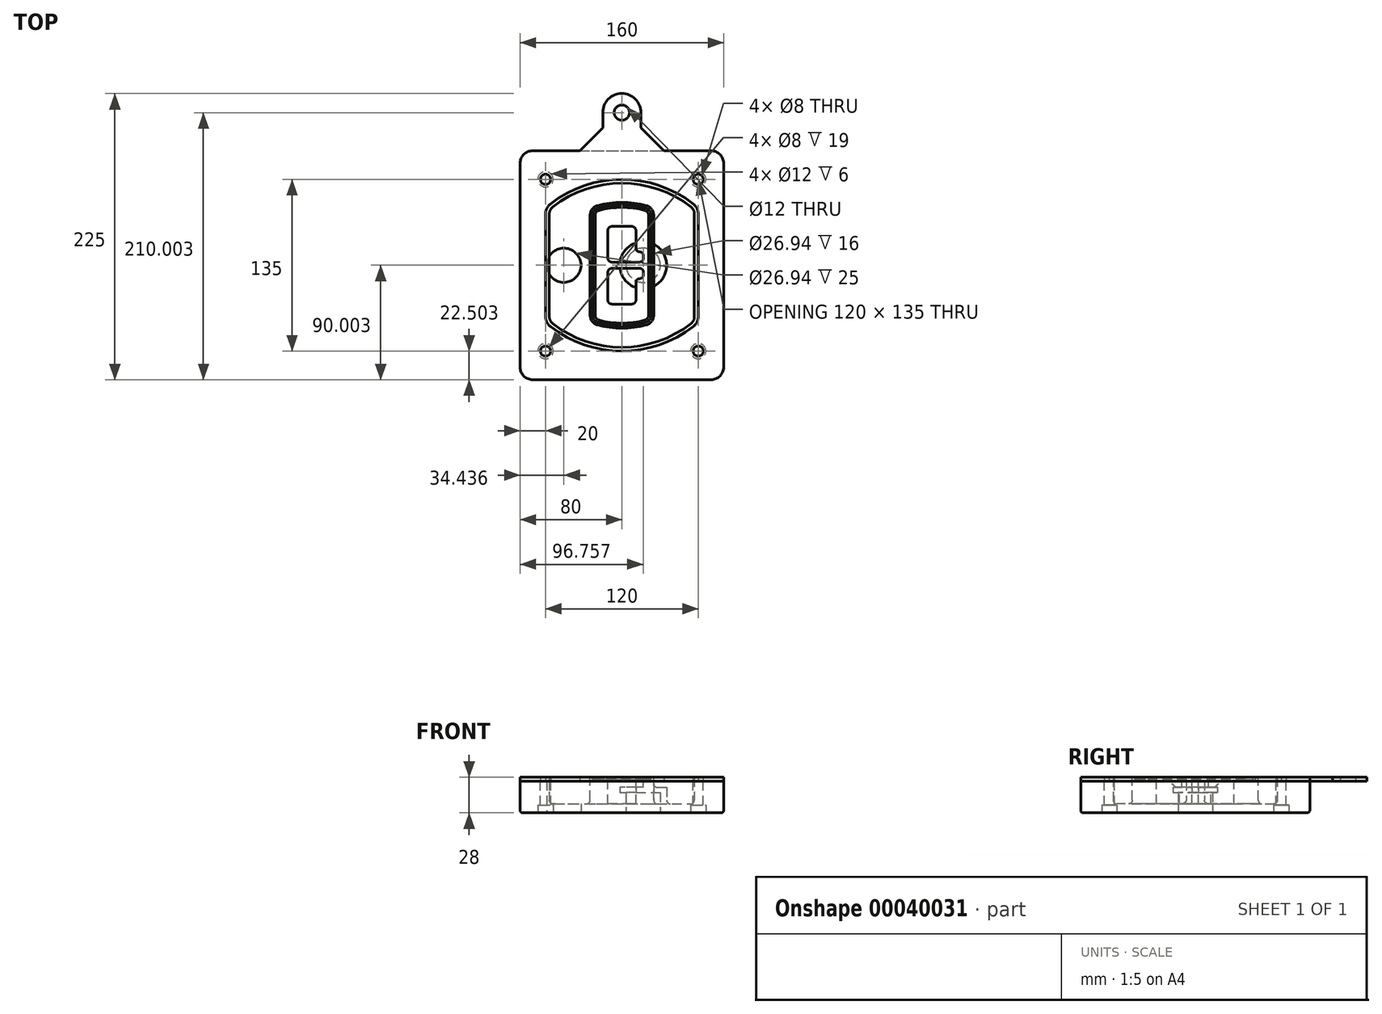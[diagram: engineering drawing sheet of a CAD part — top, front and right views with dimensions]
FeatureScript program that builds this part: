
annotation { "Feature Type Name" : "Feature", "Feature Type Description" : "" }
export const myFeature = defineFeature(function(context is Context, id is Id, definition is map)
    precondition{}
    {
        {
            var Q0;
            Q0=qCreatedBy(makeId("Top.planeOp"),FACE);
            var sketch = newSketch(context, id + "F0", { "sketchPlane" : qUnion([Q0])});
            skPoint(sketch, "E0.rect.middle", {"position": v(0, 0) * mm});
            skLineSegment(sketch, "E1.bottom", {"start": v(24.05, 28.38) * mm, "end": v(164.05, 28.38) * mm});
            skLineSegment(sketch, "E1.top", {"start": v(24.05, 208.38) * mm, "end": v(164.05, 208.38) * mm});
            skLineSegment(sketch, "E1.left", {"start": v(14.05, 38.38) * mm, "end": v(14.05, 198.38) * mm});
            skLineSegment(sketch, "E1.right", {"start": v(174.05, 38.38) * mm, "end": v(174.05, 198.38) * mm});
            skLineSegment(sketch, "E2", {"start": v(14.05, 208.38) * mm, "end": v(174.05, 28.38) * mm, "construction": true});
            skLineSegment(sketch, "E3", {"start": v(174.05, 208.38) * mm, "end": v(14.05, 28.38) * mm, "construction": true});
            skCircle(sketch, "E4", {"center": v(34.05, 185.88) * mm, "radius": 4 * mm});
            skCircle(sketch, "E5", {"center": v(154.05, 185.88) * mm, "radius": 4 * mm});
            skCircle(sketch, "E6", {"center": v(154.05, 50.88) * mm, "radius": 4 * mm});
            skCircle(sketch, "E7", {"center": v(34.05, 50.88) * mm, "radius": 4 * mm});
            skLineSegment(sketch, "E8", {"start": v(34.05, 185.88) * mm, "end": v(154.05, 185.88) * mm, "construction": true});
            skLineSegment(sketch, "E9", {"start": v(154.05, 185.88) * mm, "end": v(154.05, 50.88) * mm, "construction": true});
            skLineSegment(sketch, "E10", {"start": v(154.05, 50.88) * mm, "end": v(34.05, 50.88) * mm, "construction": true});
            skLineSegment(sketch, "E11", {"start": v(34.05, 50.88) * mm, "end": v(34.05, 185.88) * mm, "construction": true});
            skLineSegment(sketch, "E12", {"start": v(34.05, 158.68) * mm, "end": v(34.05, 78.09) * mm});
            skLineSegment(sketch, "E13", {"start": v(154.05, 158.68) * mm, "end": v(154.05, 78.09) * mm});
            skArc(sketch, "E14", {"start": v(150.2, 166.56) * mm, "mid": v(94.05, 185.88) * mm, "end": v(37.9, 166.56) * mm});
            skArc(sketch, "E15", {"start": v(37.9, 70.2) * mm, "mid": v(94.05, 50.88) * mm, "end": v(150.2, 70.2) * mm});
            skLineSegment(sketch, "E16", {"start": v(34.05, 118.38) * mm, "end": v(154.05, 118.38) * mm, "construction": true});
            skPoint(sketch, "E17.visualSharp", {"position": v(34.05, 73.38) * mm});
            skArc(sketch, "E17.filletArc", {"start": v(34.05, 78.09) * mm, "mid": v(35.06, 73.7) * mm, "end": v(37.9, 70.2) * mm});
            skPoint(sketch, "E18.visualSharp", {"position": v(34.05, 163.38) * mm});
            skArc(sketch, "E18.filletArc", {"start": v(37.9, 166.56) * mm, "mid": v(35.06, 163.06) * mm, "end": v(34.05, 158.68) * mm});
            skPoint(sketch, "E19.visualSharp", {"position": v(154.05, 163.38) * mm});
            skArc(sketch, "E19.filletArc", {"start": v(154.05, 158.68) * mm, "mid": v(153.04, 163.06) * mm, "end": v(150.2, 166.56) * mm});
            skPoint(sketch, "E20.visualSharp", {"position": v(154.05, 73.38) * mm});
            skArc(sketch, "E20.filletArc", {"start": v(150.2, 70.2) * mm, "mid": v(153.04, 73.7) * mm, "end": v(154.05, 78.09) * mm});
            skPoint(sketch, "E21.visualSharp", {"position": v(14.05, 208.38) * mm});
            skArc(sketch, "E21.filletArc", {"start": v(24.05, 208.38) * mm, "mid": v(16.98, 205.45) * mm, "end": v(14.05, 198.38) * mm});
            skPoint(sketch, "E22.visualSharp", {"position": v(174.05, 208.38) * mm});
            skArc(sketch, "E22.filletArc", {"start": v(174.05, 198.38) * mm, "mid": v(171.12, 205.45) * mm, "end": v(164.05, 208.38) * mm});
            skPoint(sketch, "E23.visualSharp", {"position": v(174.05, 28.38) * mm});
            skArc(sketch, "E23.filletArc", {"start": v(164.05, 28.38) * mm, "mid": v(171.12, 31.31) * mm, "end": v(174.05, 38.38) * mm});
            skPoint(sketch, "E24.visualSharp", {"position": v(14.05, 28.38) * mm});
            skArc(sketch, "E24.filletArc", {"start": v(14.05, 38.38) * mm, "mid": v(16.98, 31.31) * mm, "end": v(24.05, 28.38) * mm});
            skArc(sketch, "E25.0", {"start": v(151.05, 158.68) * mm, "mid": v(150.34, 161.75) * mm, "end": v(148.36, 164.2) * mm});
            skLineSegment(sketch, "E25.1", {"start": v(151.05, 158.68) * mm, "end": v(151.05, 78.09) * mm});
            skArc(sketch, "E25.2", {"start": v(148.36, 72.57) * mm, "mid": v(150.34, 75.02) * mm, "end": v(151.05, 78.09) * mm});
            skArc(sketch, "E25.3", {"start": v(39.74, 72.57) * mm, "mid": v(94.05, 53.88) * mm, "end": v(148.36, 72.57) * mm});
            skArc(sketch, "E25.4", {"start": v(37.05, 78.09) * mm, "mid": v(37.76, 75.02) * mm, "end": v(39.74, 72.57) * mm});
            skArc(sketch, "E25.5", {"start": v(148.36, 164.2) * mm, "mid": v(94.05, 182.88) * mm, "end": v(39.74, 164.2) * mm});
            skLineSegment(sketch, "E25.6", {"start": v(37.05, 158.68) * mm, "end": v(37.05, 78.09) * mm});
            skArc(sketch, "E25.7", {"start": v(39.74, 164.2) * mm, "mid": v(37.76, 161.75) * mm, "end": v(37.05, 158.68) * mm});
            skArc(sketch, "E26.0", {"start": v(35.43, 169.71) * mm, "mid": v(31.47, 164.82) * mm, "end": v(30.05, 158.68) * mm});
            skArc(sketch, "E26.1", {"start": v(152.67, 169.71) * mm, "mid": v(94.05, 189.88) * mm, "end": v(35.43, 169.71) * mm});
            skArc(sketch, "E26.2", {"start": v(158.05, 158.68) * mm, "mid": v(156.63, 164.82) * mm, "end": v(152.67, 169.71) * mm});
            skLineSegment(sketch, "E26.3", {"start": v(158.05, 158.68) * mm, "end": v(158.05, 78.09) * mm});
            skArc(sketch, "E26.4", {"start": v(152.67, 67.05) * mm, "mid": v(156.63, 71.95) * mm, "end": v(158.05, 78.09) * mm});
            skLineSegment(sketch, "E26.5", {"start": v(30.05, 158.68) * mm, "end": v(30.05, 78.09) * mm});
            skArc(sketch, "E26.6", {"start": v(35.43, 67.05) * mm, "mid": v(94.05, 46.88) * mm, "end": v(152.67, 67.05) * mm});
            skArc(sketch, "E26.7", {"start": v(30.05, 78.09) * mm, "mid": v(31.47, 71.95) * mm, "end": v(35.43, 67.05) * mm});
            skSolve(sketch);
        }
        {
            var Q0;
            Q0=makeQuery(id+"F0.imprint","IMPRINT",FACE,{"disambiguationData":[TD([[makeQuery(id+"F0.imprint","IMPRINT",EDGE,{"derivedFrom":sQuery(id+"F0.wireOp",EDGE,"E1.bottom")}),1.0]])]});
            var Q1;
            Q1=makeQuery(id+"F0.imprint","IMPRINT",FACE,{"disambiguationData":[TD([[makeQuery(id+"F0.imprint","IMPRINT",EDGE,{"derivedFrom":sQuery(id+"F0.wireOp",EDGE,"E12")}),1.0]])]});
            var Q2;
            Q2=makeQuery(id+"F0.imprint","IMPRINT",FACE,{"disambiguationData":[TD([[makeQuery(id+"F0.imprint","IMPRINT",EDGE,{"derivedFrom":sQuery(id+"F0.wireOp",EDGE,"E25.0")}),1.0]])]});
            var Q3;
            Q3=makeQuery(id+"F0.imprint","IMPRINT",FACE,{"disambiguationData":[TD([[makeQuery(id+"F0.imprint","IMPRINT",EDGE,{"derivedFrom":sQuery(id+"F0.wireOp",EDGE,"E12")}),-1.0]])]});
            extrude(context, id + "F1", {"entities" : qUnion([Q0, Q1, Q2, Q3]), "oppositeDirection" : true, "depth" : 25 * mm});
        }
        {
            var Q0;
            Q0=makeQuery(id+"F0.imprint","IMPRINT",FACE,{"disambiguationData":[TD([[makeQuery(id+"F0.imprint","IMPRINT",EDGE,{"derivedFrom":sQuery(id+"F0.wireOp",EDGE,"E12")}),1.0]])]});
            extrude(context, id + "F2", {"entities" : qUnion([Q0]), "operationType" : NewBodyOperationType.ADD, "depth" : 3 * mm});
        }
        {
            var Q0;
            Q0=makeQuery(id+"F0.imprint","IMPRINT",FACE,{"disambiguationData":[TD([[makeQuery(id+"F0.imprint","IMPRINT",EDGE,{"derivedFrom":sQuery(id+"F0.wireOp",EDGE,"E25.0")}),1.0]])]});
            extrude(context, id + "F3", {"entities" : qUnion([Q0]), "operationType" : NewBodyOperationType.REMOVE, "oppositeDirection" : true, "depth" : 18 * mm});
        }
        {
            var Q0;
            Q0=makeQuery(id+"F2.opExtrude","CAP_FACE",FACE,{"disambiguationData":[OSD([sQuery(id+"F0.wireOp",EDGE,"E12"),sQuery(id+"F0.wireOp",EDGE,"E13"),sQuery(id+"F0.wireOp",EDGE,"E14"),sQuery(id+"F0.wireOp",EDGE,"E15"),sQuery(id+"F0.wireOp",EDGE,"E17.filletArc"),sQuery(id+"F0.wireOp",EDGE,"E18.filletArc"),sQuery(id+"F0.wireOp",EDGE,"E19.filletArc"),sQuery(id+"F0.wireOp",EDGE,"E20.filletArc"),sQuery(id+"F0.wireOp",EDGE,"E25.0"),sQuery(id+"F0.wireOp",EDGE,"E25.1"),sQuery(id+"F0.wireOp",EDGE,"E25.2"),sQuery(id+"F0.wireOp",EDGE,"E25.3"),sQuery(id+"F0.wireOp",EDGE,"E25.4"),sQuery(id+"F0.wireOp",EDGE,"E25.5"),sQuery(id+"F0.wireOp",EDGE,"E25.6"),sQuery(id+"F0.wireOp",EDGE,"E25.7")])],"isStart":false});
            var sketch = newSketch(context, id + "F4", { "sketchPlane" : qUnion([Q0])});
            skArc(sketch, "E27.0", {"start": v(74.97, 71.41) * mm, "mid": v(94.05, 68.88) * mm, "end": v(113.13, 71.41) * mm});
            skArc(sketch, "E28.0", {"start": v(113.13, 165.35) * mm, "mid": v(94.05, 167.88) * mm, "end": v(74.97, 165.35) * mm});
            skLineSegment(sketch, "E29", {"start": v(69.05, 157.63) * mm, "end": v(69.05, 79.14) * mm});
            skLineSegment(sketch, "E30", {"start": v(119.05, 157.63) * mm, "end": v(119.05, 79.14) * mm});
            skLineSegment(sketch, "E31", {"start": v(69.05, 163.48) * mm, "end": v(119.05, 163.48) * mm, "construction": true});
            skLineSegment(sketch, "E32", {"start": v(69.05, 73.28) * mm, "end": v(119.05, 73.28) * mm, "construction": true});
            skPoint(sketch, "E33.visualSharp", {"position": v(69.05, 163.48) * mm});
            skArc(sketch, "E33.filletArc", {"start": v(74.97, 165.35) * mm, "mid": v(70.7, 162.5) * mm, "end": v(69.05, 157.63) * mm});
            skPoint(sketch, "E34.visualSharp", {"position": v(119.05, 163.48) * mm});
            skArc(sketch, "E34.filletArc", {"start": v(119.05, 157.63) * mm, "mid": v(117.4, 162.5) * mm, "end": v(113.13, 165.35) * mm});
            skPoint(sketch, "E35.visualSharp", {"position": v(119.05, 73.28) * mm});
            skArc(sketch, "E35.filletArc", {"start": v(113.13, 71.41) * mm, "mid": v(117.4, 74.27) * mm, "end": v(119.05, 79.14) * mm});
            skPoint(sketch, "E36.visualSharp", {"position": v(69.05, 73.28) * mm});
            skArc(sketch, "E36.filletArc", {"start": v(69.05, 79.14) * mm, "mid": v(70.7, 74.27) * mm, "end": v(74.97, 71.41) * mm});
            skArc(sketch, "E37.0", {"start": v(148.36, 164.2) * mm, "mid": v(94.05, 182.88) * mm, "end": v(39.74, 164.2) * mm});
            skArc(sketch, "E37.1", {"start": v(39.74, 164.2) * mm, "mid": v(37.76, 161.75) * mm, "end": v(37.05, 158.68) * mm});
            skLineSegment(sketch, "E37.2", {"start": v(37.05, 158.68) * mm, "end": v(37.05, 78.09) * mm});
            skArc(sketch, "E37.3", {"start": v(37.05, 78.09) * mm, "mid": v(37.76, 75.02) * mm, "end": v(39.74, 72.57) * mm});
            skArc(sketch, "E37.4", {"start": v(39.74, 72.57) * mm, "mid": v(94.05, 53.88) * mm, "end": v(148.36, 72.57) * mm});
            skArc(sketch, "E37.5", {"start": v(148.36, 72.57) * mm, "mid": v(150.34, 75.02) * mm, "end": v(151.05, 78.09) * mm});
            skLineSegment(sketch, "E37.6", {"start": v(151.05, 158.68) * mm, "end": v(151.05, 78.09) * mm});
            skArc(sketch, "E37.7", {"start": v(151.05, 158.68) * mm, "mid": v(150.34, 161.75) * mm, "end": v(148.36, 164.2) * mm});
            skLineSegment(sketch, "E38.0", {"start": v(117.05, 157.63) * mm, "end": v(117.05, 79.14) * mm});
            skArc(sketch, "E38.1", {"start": v(112.61, 73.34) * mm, "mid": v(115.81, 75.49) * mm, "end": v(117.05, 79.14) * mm});
            skArc(sketch, "E38.2", {"start": v(75.49, 73.34) * mm, "mid": v(94.05, 70.88) * mm, "end": v(112.61, 73.34) * mm});
            skArc(sketch, "E38.3", {"start": v(71.05, 79.14) * mm, "mid": v(72.29, 75.49) * mm, "end": v(75.49, 73.34) * mm});
            skLineSegment(sketch, "E38.4", {"start": v(71.05, 157.63) * mm, "end": v(71.05, 79.14) * mm});
            skArc(sketch, "E38.5", {"start": v(117.05, 157.63) * mm, "mid": v(115.81, 161.28) * mm, "end": v(112.61, 163.42) * mm});
            skArc(sketch, "E38.6", {"start": v(75.49, 163.42) * mm, "mid": v(72.29, 161.28) * mm, "end": v(71.05, 157.63) * mm});
            skArc(sketch, "E38.7", {"start": v(112.61, 163.42) * mm, "mid": v(94.05, 165.88) * mm, "end": v(75.49, 163.42) * mm});
            skArc(sketch, "E39.0", {"start": v(115.05, 157.63) * mm, "mid": v(114.23, 160.06) * mm, "end": v(112.1, 161.5) * mm});
            skLineSegment(sketch, "E39.1", {"start": v(115.05, 157.63) * mm, "end": v(115.05, 79.14) * mm});
            skArc(sketch, "E39.2", {"start": v(112.1, 75.27) * mm, "mid": v(114.23, 76.7) * mm, "end": v(115.05, 79.14) * mm});
            skArc(sketch, "E39.3", {"start": v(76, 75.27) * mm, "mid": v(94.05, 72.88) * mm, "end": v(112.1, 75.27) * mm});
            skArc(sketch, "E39.4", {"start": v(73.05, 79.14) * mm, "mid": v(73.87, 76.7) * mm, "end": v(76, 75.27) * mm});
            skArc(sketch, "E39.5", {"start": v(112.1, 161.5) * mm, "mid": v(94.05, 163.88) * mm, "end": v(76, 161.5) * mm});
            skLineSegment(sketch, "E39.6", {"start": v(73.05, 157.63) * mm, "end": v(73.05, 79.14) * mm});
            skArc(sketch, "E39.7", {"start": v(76, 161.5) * mm, "mid": v(73.87, 160.06) * mm, "end": v(73.05, 157.63) * mm});
            skLineSegment(sketch, "E40", {"start": v(69.05, 118.38) * mm, "end": v(119.05, 118.38) * mm, "construction": true});
            skLineSegment(sketch, "E41", {"start": v(83.05, 123.88) * mm, "end": v(83.05, 145.88) * mm});
            skLineSegment(sketch, "E42", {"start": v(86.05, 148.88) * mm, "end": v(102.05, 148.88) * mm});
            skLineSegment(sketch, "E43", {"start": v(105.05, 145.88) * mm, "end": v(105.05, 131.88) * mm});
            skLineSegment(sketch, "E44", {"start": v(108.05, 128.88) * mm, "end": v(108.05, 128.88) * mm});
            skLineSegment(sketch, "E45", {"start": v(111.05, 125.88) * mm, "end": v(111.05, 123.88) * mm});
            skLineSegment(sketch, "E46", {"start": v(108.05, 120.88) * mm, "end": v(86.05, 120.88) * mm});
            skPoint(sketch, "E47.visualSharp", {"position": v(83.05, 148.88) * mm});
            skArc(sketch, "E47.filletArc", {"start": v(86.05, 148.88) * mm, "mid": v(83.93, 148) * mm, "end": v(83.05, 145.88) * mm});
            skPoint(sketch, "E48.visualSharp", {"position": v(105.05, 148.88) * mm});
            skArc(sketch, "E48.filletArc", {"start": v(105.05, 145.88) * mm, "mid": v(104.17, 148) * mm, "end": v(102.05, 148.88) * mm});
            skPoint(sketch, "E49.visualSharp", {"position": v(105.05, 128.88) * mm});
            skArc(sketch, "E49.filletArc", {"start": v(105.05, 131.88) * mm, "mid": v(105.93, 129.76) * mm, "end": v(108.05, 128.88) * mm});
            skPoint(sketch, "E50.visualSharp", {"position": v(111.05, 128.88) * mm});
            skArc(sketch, "E50.filletArc", {"start": v(111.05, 125.88) * mm, "mid": v(110.17, 128) * mm, "end": v(108.05, 128.88) * mm});
            skPoint(sketch, "E51.visualSharp", {"position": v(111.05, 120.88) * mm});
            skArc(sketch, "E51.filletArc", {"start": v(108.05, 120.88) * mm, "mid": v(110.17, 121.76) * mm, "end": v(111.05, 123.88) * mm});
            skPoint(sketch, "E52.visualSharp", {"position": v(83.05, 120.88) * mm});
            skArc(sketch, "E52.filletArc", {"start": v(83.05, 123.88) * mm, "mid": v(83.93, 121.76) * mm, "end": v(86.05, 120.88) * mm});
            skLineSegment(sketch, "E53.0.MirrorCS", {"start": v(108.05, 115.88) * mm, "end": v(86.05, 115.88) * mm});
            skArc(sketch, "E54.0.MirrorCS", {"start": v(83.05, 112.88) * mm, "mid": v(83.93, 115) * mm, "end": v(86.05, 115.88) * mm});
            skLineSegment(sketch, "E55.0.MirrorCS", {"start": v(83.05, 112.88) * mm, "end": v(83.05, 90.88) * mm});
            skArc(sketch, "E56.0.MirrorCS", {"start": v(86.05, 87.88) * mm, "mid": v(83.93, 88.76) * mm, "end": v(83.05, 90.88) * mm});
            skLineSegment(sketch, "E57.0.MirrorCS", {"start": v(86.05, 87.88) * mm, "end": v(102.05, 87.88) * mm});
            skArc(sketch, "E58.0.MirrorCS", {"start": v(105.05, 90.88) * mm, "mid": v(104.17, 88.76) * mm, "end": v(102.05, 87.88) * mm});
            skLineSegment(sketch, "E59.0.MirrorCS", {"start": v(105.05, 90.88) * mm, "end": v(105.05, 104.88) * mm});
            skArc(sketch, "E60.0.MirrorCS", {"start": v(105.05, 104.88) * mm, "mid": v(105.93, 107) * mm, "end": v(108.05, 107.88) * mm});
            skArc(sketch, "E61.0.MirrorCS", {"start": v(111.05, 110.88) * mm, "mid": v(110.17, 108.76) * mm, "end": v(108.05, 107.88) * mm});
            skLineSegment(sketch, "E62.0.MirrorCS", {"start": v(111.05, 110.88) * mm, "end": v(111.05, 112.88) * mm});
            skArc(sketch, "E63.0.MirrorCS", {"start": v(108.05, 115.88) * mm, "mid": v(110.17, 115) * mm, "end": v(111.05, 112.88) * mm});
            skSolve(sketch);
        }
        {
            var Q0;
            Q0=makeQuery(id+"F4.imprint","IMPRINT",FACE,{"disambiguationData":[TD([[makeQuery(id+"F4.imprint","IMPRINT",EDGE,{"derivedFrom":sQuery(id+"F4.wireOp",EDGE,"E27.0")}),1.0]])]});
            var Q1;
            Q1=makeQuery(id+"F4.imprint","IMPRINT",FACE,{"disambiguationData":[TD([[makeQuery(id+"F4.imprint","IMPRINT",EDGE,{"derivedFrom":sQuery(id+"F4.wireOp",EDGE,"E38.0")}),-1.0]])]});
            var Q2;
            Q2=makeQuery(id+"F4.imprint","IMPRINT",FACE,{"disambiguationData":[TD([[makeQuery(id+"F4.imprint","IMPRINT",EDGE,{"derivedFrom":sQuery(id+"F4.wireOp",EDGE,"E39.0")}),1.0]])]});
            extrude(context, id + "F5", {"entities" : qUnion([Q0, Q1, Q2]), "operationType" : NewBodyOperationType.ADD, "endBound" : BoundingType.UP_TO_NEXT, "oppositeDirection" : true, "depth" : 25 * mm});
        }
        {
            var Q0;
            Q0=makeQuery(id+"F4.imprint","IMPRINT",FACE,{"disambiguationData":[TD([[makeQuery(id+"F4.imprint","IMPRINT",EDGE,{"derivedFrom":sQuery(id+"F4.wireOp",EDGE,"E38.0")}),-1.0]])]});
            extrude(context, id + "F6", {"entities" : qUnion([Q0]), "operationType" : NewBodyOperationType.REMOVE, "oppositeDirection" : true, "depth" : 2 * mm});
        }
        {
            var Q0;
            Q0=makeQuery(id+"F1.opExtrude","CAP_FACE",FACE,{"disambiguationData":[OSD([sQuery(id+"F0.wireOp",EDGE,"E1.bottom"),sQuery(id+"F0.wireOp",EDGE,"E1.top"),sQuery(id+"F0.wireOp",EDGE,"E1.left"),sQuery(id+"F0.wireOp",EDGE,"E1.right"),sQuery(id+"F0.wireOp",EDGE,"E4"),sQuery(id+"F0.wireOp",EDGE,"E5"),sQuery(id+"F0.wireOp",EDGE,"E6"),sQuery(id+"F0.wireOp",EDGE,"E7"),sQuery(id+"F0.wireOp",EDGE,"E21.filletArc"),sQuery(id+"F0.wireOp",EDGE,"E22.filletArc"),sQuery(id+"F0.wireOp",EDGE,"E23.filletArc"),sQuery(id+"F0.wireOp",EDGE,"E24.filletArc")])],"isStart":false});
            var sketch = newSketch(context, id + "F7", { "sketchPlane" : qUnion([Q0])});
            skCircle(sketch, "E64", {"center": v(110.8, -118.38) * mm, "radius": 13.47 * mm});
            skCircle(sketch, "E65", {"center": v(48.49, -118.38) * mm, "radius": 13.47 * mm});
            skLineSegment(sketch, "E66", {"start": v(174.05, -118.38) * mm, "end": v(14.05, -118.38) * mm});
            skCircle(sketch, "E67", {"center": v(110.8, -118.38) * mm, "radius": 18.47 * mm});
            skCircle(sketch, "E68", {"center": v(154.05, -185.88) * mm, "radius": 6 * mm});
            skCircle(sketch, "E69", {"center": v(34.05, -185.88) * mm, "radius": 6 * mm});
            skCircle(sketch, "E70", {"center": v(34.05, -50.88) * mm, "radius": 6 * mm});
            skCircle(sketch, "E71", {"center": v(154.05, -50.88) * mm, "radius": 6 * mm});
            skSolve(sketch);
        }
        {
            var Q0;
            {var subQ1=sQuery(id+"F7.wireOp",EDGE,"E66");var subQ4=sQuery(id+"F7.wireOp",EDGE,"E64");var subQ6=makeQuery(id+"F7.imprint","INTERSECT",VERTEX,{"disambiguationData":[OD(0.0)],"derivedFrom":[subQ4,subQ1]});Q0=makeQuery(id+"F7.imprint","IMPRINT",FACE,{"disambiguationData":[TD([[makeQuery(id+"F7.imprint","IMPRINT",EDGE,{"disambiguationData":[TD([[subQ6,-1.0]])],"derivedFrom":subQ4}),-1.0]])]});}
            var Q1;
            {var subQ0=sQuery(id+"F7.wireOp",EDGE,"E66");var subQ1=sQuery(id+"F7.wireOp",EDGE,"E64");var subQ3=makeQuery(id+"F7.imprint","INTERSECT",VERTEX,{"disambiguationData":[OD(0.0)],"derivedFrom":[subQ1,subQ0]});Q1=makeQuery(id+"F7.imprint","IMPRINT",FACE,{"disambiguationData":[TD([[makeQuery(id+"F7.imprint","IMPRINT",EDGE,{"disambiguationData":[TD([[subQ3,-1.0]])],"derivedFrom":subQ1}),1.0]])]});}
            var Q2;
            {var subQ0=sQuery(id+"F7.wireOp",EDGE,"E66");var subQ1=sQuery(id+"F7.wireOp",EDGE,"E64");var subQ3=makeQuery(id+"F7.imprint","INTERSECT",VERTEX,{"disambiguationData":[OD(0.0)],"derivedFrom":[subQ1,subQ0]});Q2=makeQuery(id+"F7.imprint","IMPRINT",FACE,{"disambiguationData":[TD([[makeQuery(id+"F7.imprint","IMPRINT",EDGE,{"disambiguationData":[TD([[subQ3,1.0]])],"derivedFrom":subQ1}),1.0]])]});}
            var Q3;
            {var subQ1=sQuery(id+"F7.wireOp",EDGE,"E66");var subQ4=sQuery(id+"F7.wireOp",EDGE,"E64");var subQ6=makeQuery(id+"F7.imprint","INTERSECT",VERTEX,{"disambiguationData":[OD(0.0)],"derivedFrom":[subQ4,subQ1]});Q3=makeQuery(id+"F7.imprint","IMPRINT",FACE,{"disambiguationData":[TD([[makeQuery(id+"F7.imprint","IMPRINT",EDGE,{"disambiguationData":[TD([[subQ6,1.0]])],"derivedFrom":subQ4}),-1.0]])]});}
            extrude(context, id + "F8", {"entities" : qUnion([Q0, Q1, Q2, Q3]), "operationType" : NewBodyOperationType.ADD, "oppositeDirection" : true, "depth" : 20 * mm});
        }
        {
            var Q0;
            {var subQ0=sQuery(id+"F7.wireOp",EDGE,"E66");var subQ1=sQuery(id+"F7.wireOp",EDGE,"E64");var subQ3=makeQuery(id+"F7.imprint","INTERSECT",VERTEX,{"disambiguationData":[OD(0.0)],"derivedFrom":[subQ1,subQ0]});Q0=makeQuery(id+"F7.imprint","IMPRINT",FACE,{"disambiguationData":[TD([[makeQuery(id+"F7.imprint","IMPRINT",EDGE,{"disambiguationData":[TD([[subQ3,-1.0]])],"derivedFrom":subQ1}),1.0]])]});}
            var Q1;
            {var subQ0=sQuery(id+"F7.wireOp",EDGE,"E66");var subQ1=sQuery(id+"F7.wireOp",EDGE,"E64");var subQ3=makeQuery(id+"F7.imprint","INTERSECT",VERTEX,{"disambiguationData":[OD(0.0)],"derivedFrom":[subQ1,subQ0]});Q1=makeQuery(id+"F7.imprint","IMPRINT",FACE,{"disambiguationData":[TD([[makeQuery(id+"F7.imprint","IMPRINT",EDGE,{"disambiguationData":[TD([[subQ3,1.0]])],"derivedFrom":subQ1}),1.0]])]});}
            extrude(context, id + "F9", {"entities" : qUnion([Q0, Q1]), "operationType" : NewBodyOperationType.REMOVE, "oppositeDirection" : true, "depth" : 16 * mm});
        }
        {
            var Q0;
            {var subQ0=sQuery(id+"F7.wireOp",EDGE,"E66");var subQ1=sQuery(id+"F7.wireOp",EDGE,"E65");var subQ3=makeQuery(id+"F7.imprint","INTERSECT",VERTEX,{"disambiguationData":[OD(0.0)],"derivedFrom":[subQ1,subQ0]});Q0=makeQuery(id+"F7.imprint","IMPRINT",FACE,{"disambiguationData":[TD([[makeQuery(id+"F7.imprint","IMPRINT",EDGE,{"disambiguationData":[TD([[subQ3,-1.0]])],"derivedFrom":subQ1}),1.0]])]});}
            var Q1;
            {var subQ0=sQuery(id+"F7.wireOp",EDGE,"E66");var subQ1=sQuery(id+"F7.wireOp",EDGE,"E65");var subQ3=makeQuery(id+"F7.imprint","INTERSECT",VERTEX,{"disambiguationData":[OD(0.0)],"derivedFrom":[subQ1,subQ0]});Q1=makeQuery(id+"F7.imprint","IMPRINT",FACE,{"disambiguationData":[TD([[makeQuery(id+"F7.imprint","IMPRINT",EDGE,{"disambiguationData":[TD([[subQ3,1.0]])],"derivedFrom":subQ1}),1.0]])]});}
            extrude(context, id + "F10", {"entities" : qUnion([Q0, Q1]), "operationType" : NewBodyOperationType.REMOVE, "oppositeDirection" : true, "depth" : 25 * mm});
        }
        {
            var Q0;
            Q0=makeQuery(id+"F7.imprint","IMPRINT",FACE,{"disambiguationData":[TD([[makeQuery(id+"F7.imprint","IMPRINT",EDGE,{"derivedFrom":sQuery(id+"F7.wireOp",EDGE,"E68")}),1.0]])]});
            var Q1;
            Q1=makeQuery(id+"F7.imprint","IMPRINT",FACE,{"disambiguationData":[TD([[makeQuery(id+"F7.imprint","IMPRINT",EDGE,{"derivedFrom":makeQuery(id+"F1.opExtrude","CAP_EDGE",EDGE,{"disambiguationData":[OSD([sQuery(id+"F0.wireOp",EDGE,"E5")])],"isStart":false})}),-1.0]])]});
            var Q2;
            Q2=makeQuery(id+"F7.imprint","IMPRINT",FACE,{"disambiguationData":[TD([[makeQuery(id+"F7.imprint","IMPRINT",EDGE,{"derivedFrom":sQuery(id+"F7.wireOp",EDGE,"E69")}),1.0]])]});
            var Q3;
            Q3=makeQuery(id+"F7.imprint","IMPRINT",FACE,{"disambiguationData":[TD([[makeQuery(id+"F7.imprint","IMPRINT",EDGE,{"derivedFrom":makeQuery(id+"F1.opExtrude","CAP_EDGE",EDGE,{"disambiguationData":[OSD([sQuery(id+"F0.wireOp",EDGE,"E4")])],"isStart":false})}),-1.0]])]});
            var Q4;
            Q4=makeQuery(id+"F7.imprint","IMPRINT",FACE,{"disambiguationData":[TD([[makeQuery(id+"F7.imprint","IMPRINT",EDGE,{"derivedFrom":sQuery(id+"F7.wireOp",EDGE,"E70")}),1.0]])]});
            var Q5;
            Q5=makeQuery(id+"F7.imprint","IMPRINT",FACE,{"disambiguationData":[TD([[makeQuery(id+"F7.imprint","IMPRINT",EDGE,{"derivedFrom":makeQuery(id+"F1.opExtrude","CAP_EDGE",EDGE,{"disambiguationData":[OSD([sQuery(id+"F0.wireOp",EDGE,"E7")])],"isStart":false})}),-1.0]])]});
            var Q6;
            Q6=makeQuery(id+"F7.imprint","IMPRINT",FACE,{"disambiguationData":[TD([[makeQuery(id+"F7.imprint","IMPRINT",EDGE,{"derivedFrom":sQuery(id+"F7.wireOp",EDGE,"E71")}),1.0]])]});
            var Q7;
            Q7=makeQuery(id+"F7.imprint","IMPRINT",FACE,{"disambiguationData":[TD([[makeQuery(id+"F7.imprint","IMPRINT",EDGE,{"derivedFrom":makeQuery(id+"F1.opExtrude","CAP_EDGE",EDGE,{"disambiguationData":[OSD([sQuery(id+"F0.wireOp",EDGE,"E6")])],"isStart":false})}),-1.0]])]});
            extrude(context, id + "F11", {"entities" : qUnion([Q0, Q1, Q2, Q3, Q4, Q5, Q6, Q7]), "operationType" : NewBodyOperationType.REMOVE, "oppositeDirection" : true, "depth" : 6 * mm});
        }
        {
            var Q0;
            Q0=makeQuery(id+"F9.boolean.opBoolean","COPY",FACE,{"derivedFrom":makeQuery(id+"F9.opExtrude","CAP_FACE",FACE,{"disambiguationData":[OSD([sQuery(id+"F7.wireOp",EDGE,"E64")])],"isStart":false})});
            var sketch = newSketch(context, id + "F12", { "sketchPlane" : qUnion([Q0])});
            skArc(sketch, "E72.0", {"start": v(105.05, -100.83) * mm, "mid": v(96.62, -106.56) * mm, "end": v(92.5, -115.88) * mm});
            skArc(sketch, "E72.1", {"start": v(92.5, -120.88) * mm, "mid": v(96.62, -130.2) * mm, "end": v(105.05, -135.93) * mm});
            skLineSegment(sketch, "E73", {"start": v(92.5, -120.88) * mm, "end": v(108.05, -120.88) * mm});
            skLineSegment(sketch, "E74.0", {"start": v(108.05, -115.88) * mm, "end": v(92.5, -115.88) * mm});
            skArc(sketch, "E74.1", {"start": v(108.05, -115.88) * mm, "mid": v(110.17, -115) * mm, "end": v(111.05, -112.88) * mm});
            skLineSegment(sketch, "E74.2", {"start": v(111.05, -110.88) * mm, "end": v(111.05, -112.88) * mm});
            skArc(sketch, "E74.3", {"start": v(111.05, -110.88) * mm, "mid": v(110.17, -108.76) * mm, "end": v(108.05, -107.88) * mm});
            skArc(sketch, "E74.4", {"start": v(105.05, -104.88) * mm, "mid": v(105.93, -107) * mm, "end": v(108.05, -107.88) * mm});
            skLineSegment(sketch, "E74.5", {"start": v(105.05, -100.83) * mm, "end": v(105.05, -104.88) * mm});
            skLineSegment(sketch, "E74.7", {"start": v(108.05, -120.88) * mm, "end": v(92.5, -120.88) * mm});
            skArc(sketch, "E74.8", {"start": v(108.05, -120.88) * mm, "mid": v(110.17, -121.76) * mm, "end": v(111.05, -123.88) * mm});
            skLineSegment(sketch, "E74.9", {"start": v(111.05, -125.88) * mm, "end": v(111.05, -123.88) * mm});
            skArc(sketch, "E74.10", {"start": v(111.05, -125.88) * mm, "mid": v(110.17, -128) * mm, "end": v(108.05, -128.88) * mm});
            skArc(sketch, "E74.11", {"start": v(105.05, -131.88) * mm, "mid": v(105.93, -129.76) * mm, "end": v(108.05, -128.88) * mm});
            skLineSegment(sketch, "E74.12", {"start": v(105.05, -135.93) * mm, "end": v(105.05, -131.88) * mm});
            skPoint(sketch, "E75.orphan", {"position": v(105.05, -145.88) * mm});
            skPoint(sketch, "E76.orphan", {"position": v(86.05, -120.88) * mm});
            skPoint(sketch, "E77.orphan", {"position": v(86.05, -115.88) * mm});
            skPoint(sketch, "E78.orphan", {"position": v(105.05, -90.88) * mm});
            skSolve(sketch);
        }
        {
            var Q0;
            {var subQ7=sQuery(id+"F12.wireOp",EDGE,"E72.0");var subQ14=sQuery(id+"F12.wireOp",EDGE,"E72.1");var subQ16=sQuery(id+"F12.wireOp",EDGE,"E74.1");var subQ18=sQuery(id+"F12.wireOp",EDGE,"E74.8");Q0=qUnion([makeQuery(id+"F12.imprint","IMPRINT",FACE,{"disambiguationData":[TD([[makeQuery(id+"F12.imprint","IMPRINT",EDGE,{"derivedFrom":subQ7}),1.0]])]}),makeQuery(id+"F12.imprint","IMPRINT",FACE,{"disambiguationData":[TD([[makeQuery(id+"F12.imprint","IMPRINT",EDGE,{"derivedFrom":subQ14}),1.0]])]}),makeQuery(id+"F12.imprint","IMPRINT",FACE,{"disambiguationData":[TD([[makeQuery(id+"F12.imprint","IMPRINT",EDGE,{"derivedFrom":subQ16}),1.0]])]}),makeQuery(id+"F12.imprint","IMPRINT",FACE,{"disambiguationData":[TD([[makeQuery(id+"F12.imprint","IMPRINT",EDGE,{"derivedFrom":subQ18}),-1.0]])]})]);}
            var Q1;
            Q1=makeQuery(id+"F5.boolean.opBoolean","SPLIT",FACE,{"disambiguationData":[TD([makeQuery(id+"F5.opExtrude","SWEPT_FACE",FACE,{"disambiguationData":[OSD([sQuery(id+"F4.wireOp",EDGE,"E41")])]})])],"derivedFrom":makeQuery(id+"F3.boolean.opBoolean","COPY",FACE,{"derivedFrom":makeQuery(id+"F3.opExtrude","CAP_FACE",FACE,{"disambiguationData":[OSD([sQuery(id+"F0.wireOp",EDGE,"E25.0"),sQuery(id+"F0.wireOp",EDGE,"E25.1"),sQuery(id+"F0.wireOp",EDGE,"E25.2"),sQuery(id+"F0.wireOp",EDGE,"E25.3"),sQuery(id+"F0.wireOp",EDGE,"E25.4"),sQuery(id+"F0.wireOp",EDGE,"E25.5"),sQuery(id+"F0.wireOp",EDGE,"E25.6"),sQuery(id+"F0.wireOp",EDGE,"E25.7")])],"isStart":false})})});
            extrude(context, id + "F13", {"entities" : qUnion([Q0]), "operationType" : NewBodyOperationType.REMOVE, "endBound" : BoundingType.UP_TO_SURFACE, "endBoundEntityFace" : qUnion([Q1]), "depth" : 25 * mm});
        }
        {
            var Q0;
            Q0=makeQuery(id+"F3.boolean.opBoolean","COPY",EDGE,{"derivedFrom":makeQuery(id+"F3.opExtrude","CAP_EDGE",EDGE,{"disambiguationData":[OSD([sQuery(id+"F0.wireOp",EDGE,"E25.6")])],"isStart":false})});
            var Q1;
            Q1=makeQuery(id+"F8.boolean.opBoolean","INTERSECT",EDGE,{"derivedFrom":[makeQuery(id+"F5.opExtrude","SWEPT_FACE",FACE,{"disambiguationData":[OSD([sQuery(id+"F4.wireOp",EDGE,"E30")])]}),makeQuery(id+"F8.opExtrude","CAP_FACE",FACE,{"disambiguationData":[OSD([sQuery(id+"F7.wireOp",EDGE,"E67")])],"isStart":false})]});
            var Q2;
            Q2=makeQuery(id+"F8.boolean.opBoolean","INTERSECT",EDGE,{"disambiguationData":[OD(1.0)],"derivedFrom":[makeQuery(id+"F5.opExtrude","SWEPT_FACE",FACE,{"disambiguationData":[OSD([sQuery(id+"F4.wireOp",EDGE,"E30")])]}),makeQuery(id+"F8.opExtrude","SWEPT_FACE",FACE,{"disambiguationData":[OSD([sQuery(id+"F7.wireOp",EDGE,"E67")])]})]});
            var Q3;
            {var subQ0=sQuery(id+"F4.wireOp",EDGE,"E30");Q3=makeQuery(id+"F8.boolean.opBoolean","SPLIT",EDGE,{"disambiguationData":[TD([makeQuery(id+"F5.opExtrude","SWEPT_FACE",FACE,{"disambiguationData":[OSD([sQuery(id+"F4.wireOp",EDGE,"E35.filletArc")])]})])],"derivedFrom":makeQuery(id+"F5.opExtrude","CAP_EDGE",EDGE,{"disambiguationData":[OSD([subQ0])],"isStart":false})});}
            var Q4;
            {var subQ0=sQuery(id+"F0.wireOp",EDGE,"E25.7");var subQ1=sQuery(id+"F0.wireOp",EDGE,"E25.1");var subQ2=sQuery(id+"F0.wireOp",EDGE,"E25.6");var subQ3=sQuery(id+"F0.wireOp",EDGE,"E25.5");var subQ4=sQuery(id+"F0.wireOp",EDGE,"E25.4");var subQ5=sQuery(id+"F0.wireOp",EDGE,"E25.0");var subQ6=sQuery(id+"F0.wireOp",EDGE,"E25.2");var subQ7=sQuery(id+"F0.wireOp",EDGE,"E25.3");Q4=makeQuery(id+"F8.boolean.opBoolean","INTERSECT",EDGE,{"derivedFrom":[makeQuery(id+"F5.boolean.opBoolean","SPLIT",FACE,{"disambiguationData":[TD([makeQuery(id+"F2.opExtrude","SWEPT_FACE",FACE,{"disambiguationData":[OSD([subQ5])]})])],"derivedFrom":makeQuery(id+"F3.boolean.opBoolean","COPY",FACE,{"derivedFrom":makeQuery(id+"F3.opExtrude","CAP_FACE",FACE,{"disambiguationData":[OSD([subQ5,subQ1,subQ6,subQ7,subQ4,subQ3,subQ2,subQ0])],"isStart":false})})}),makeQuery(id+"F8.opExtrude","SWEPT_FACE",FACE,{"disambiguationData":[OSD([sQuery(id+"F7.wireOp",EDGE,"E67")])]})]});}
            var Q5;
            Q5=makeQuery(id+"F8.boolean.opBoolean","INTERSECT",EDGE,{"disambiguationData":[OD(0.0)],"derivedFrom":[makeQuery(id+"F5.opExtrude","SWEPT_FACE",FACE,{"disambiguationData":[OSD([sQuery(id+"F4.wireOp",EDGE,"E30")])]}),makeQuery(id+"F8.opExtrude","SWEPT_FACE",FACE,{"disambiguationData":[OSD([sQuery(id+"F7.wireOp",EDGE,"E67")])]})]});
            fillet(context, id + "F14", {"entities" : qUnion([Q0, Q1, Q2, Q3, Q4, Q5]), "radius" : 3 * mm, "tangentPropagation" : true, "allowEdgeOverflow" : false});
        }
        {
            var Q0;
            Q0=makeQuery(id+"F1.opExtrude","CAP_EDGE",EDGE,{"disambiguationData":[OSD([sQuery(id+"F0.wireOp",EDGE,"E1.bottom")])],"isStart":false});
            fillet(context, id + "F15", {"entities" : qUnion([Q0]), "radius" : 2 * mm, "tangentPropagation" : true, "allowEdgeOverflow" : false});
        }
        {
            var Q0;
            {var subQ0=sQuery(id+"F0.wireOp",EDGE,"E1.bottom");var subQ1=sQuery(id+"F0.wireOp",EDGE,"E1.top");var subQ2=sQuery(id+"F0.wireOp",EDGE,"E1.left");var subQ3=sQuery(id+"F0.wireOp",EDGE,"E1.right");var subQ4=sQuery(id+"F0.wireOp",EDGE,"E4");var subQ5=sQuery(id+"F0.wireOp",EDGE,"E5");var subQ6=sQuery(id+"F0.wireOp",EDGE,"E6");var subQ7=sQuery(id+"F0.wireOp",EDGE,"E7");var subQ8=sQuery(id+"F0.wireOp",EDGE,"E21.filletArc");var subQ9=sQuery(id+"F0.wireOp",EDGE,"E22.filletArc");var subQ10=sQuery(id+"F0.wireOp",EDGE,"E23.filletArc");var subQ11=sQuery(id+"F0.wireOp",EDGE,"E24.filletArc");Q0=makeQuery(id+"F2.boolean.opBoolean","SPLIT",FACE,{"disambiguationData":[TD([makeQuery(id+"F1.opExtrude","SWEPT_FACE",FACE,{"disambiguationData":[OSD([subQ0])]})])],"derivedFrom":makeQuery(id+"F1.opExtrude","CAP_FACE",FACE,{"disambiguationData":[OSD([subQ0,subQ1,subQ2,subQ3,subQ4,subQ5,subQ6,subQ7,subQ8,subQ9,subQ10,subQ11])],"isStart":true})});}
            var sketch = newSketch(context, id + "F16", { "sketchPlane" : qUnion([Q0])});
            skCircle(sketch, "E79", {"center": v(94.05, 238.38) * mm, "radius": 6 * mm});
            skLineSegment(sketch, "E80", {"start": v(61.05, 208.38) * mm, "end": v(79.05, 226.38) * mm});
            skLineSegment(sketch, "E81", {"start": v(79.05, 226.38) * mm, "end": v(79.05, 238.38) * mm});
            skLineSegment(sketch, "E82", {"start": v(109.05, 238.38) * mm, "end": v(109.05, 226.38) * mm});
            skArc(sketch, "E83", {"start": v(109.05, 238.38) * mm, "mid": v(94.05, 253.38) * mm, "end": v(79.05, 238.38) * mm});
            skLineSegment(sketch, "E84", {"start": v(61.05, 208.38) * mm, "end": v(94.05, 208.38) * mm});
            skLineSegment(sketch, "E85", {"start": v(94.05, 208.38) * mm, "end": v(127.05, 208.38) * mm});
            skLineSegment(sketch, "E86", {"start": v(94.05, 238.38) * mm, "end": v(94.05, 208.38) * mm, "construction": true});
            skLineSegment(sketch, "E87.MirrorCS", {"start": v(127.05, 208.38) * mm, "end": v(109.05, 226.38) * mm});
            skLineSegment(sketch, "E88", {"start": v(174.05, 198.38) * mm, "end": v(174.05, 38.38) * mm});
            skLineSegment(sketch, "E89", {"start": v(14.05, 198.38) * mm, "end": v(14.05, 38.38) * mm});
            skArc(sketch, "E90.0", {"start": v(24.05, 208.38) * mm, "mid": v(16.98, 205.45) * mm, "end": v(14.05, 198.38) * mm});
            skLineSegment(sketch, "E90.1", {"start": v(24.05, 208.38) * mm, "end": v(164.05, 208.38) * mm});
            skArc(sketch, "E91.0", {"start": v(174.05, 198.38) * mm, "mid": v(171.12, 205.45) * mm, "end": v(164.05, 208.38) * mm});
            skArc(sketch, "E91.2", {"start": v(164.05, 28.38) * mm, "mid": v(171.12, 31.31) * mm, "end": v(174.05, 38.38) * mm});
            skLineSegment(sketch, "E91.3", {"start": v(24.05, 28.38) * mm, "end": v(164.05, 28.38) * mm});
            skArc(sketch, "E91.4", {"start": v(14.05, 38.38) * mm, "mid": v(16.98, 31.31) * mm, "end": v(24.05, 28.38) * mm});
            skCircle(sketch, "E91.5", {"center": v(34.05, 50.88) * mm, "radius": 4 * mm});
            skCircle(sketch, "E91.6", {"center": v(154.05, 50.88) * mm, "radius": 4 * mm});
            skCircle(sketch, "E91.7", {"center": v(154.05, 185.88) * mm, "radius": 4 * mm});
            skCircle(sketch, "E91.8", {"center": v(34.05, 185.88) * mm, "radius": 4 * mm});
            skLineSegment(sketch, "E91.9", {"start": v(34.05, 158.68) * mm, "end": v(34.05, 78.09) * mm});
            skArc(sketch, "E91.10", {"start": v(150.2, 166.56) * mm, "mid": v(94.05, 185.88) * mm, "end": v(37.9, 166.56) * mm});
            skArc(sketch, "E91.11", {"start": v(37.9, 166.56) * mm, "mid": v(35.06, 163.06) * mm, "end": v(34.05, 158.68) * mm});
            skArc(sketch, "E91.12", {"start": v(154.05, 158.68) * mm, "mid": v(153.04, 163.06) * mm, "end": v(150.2, 166.56) * mm});
            skLineSegment(sketch, "E91.13", {"start": v(154.05, 158.68) * mm, "end": v(154.05, 78.09) * mm});
            skArc(sketch, "E91.14", {"start": v(150.2, 70.2) * mm, "mid": v(153.04, 73.7) * mm, "end": v(154.05, 78.09) * mm});
            skArc(sketch, "E91.15", {"start": v(37.9, 70.2) * mm, "mid": v(94.05, 50.88) * mm, "end": v(150.2, 70.2) * mm});
            skArc(sketch, "E91.16", {"start": v(34.05, 78.09) * mm, "mid": v(35.06, 73.7) * mm, "end": v(37.9, 70.2) * mm});
            skLineSegment(sketch, "E92", {"start": v(14.05, 118.38) * mm, "end": v(174.05, 118.38) * mm});
            skLineSegment(sketch, "E93.MirrorCS", {"start": v(94.05, 28.38) * mm, "end": v(127.05, 28.38) * mm, "construction": true});
            skLineSegment(sketch, "E94.MirrorCS", {"start": v(61.05, 28.38) * mm, "end": v(94.05, 28.38) * mm, "construction": true});
            skArc(sketch, "E95.MirrorCS", {"start": v(109.05, -1.62) * mm, "mid": v(94.05, -16.62) * mm, "end": v(79.05, -1.62) * mm});
            skLineSegment(sketch, "E96.MirrorCS", {"start": v(127.05, 28.38) * mm, "end": v(109.05, 10.38) * mm});
            skLineSegment(sketch, "E97.MirrorCS", {"start": v(94.05, -1.62) * mm, "end": v(94.05, 28.38) * mm});
            skLineSegment(sketch, "E98.MirrorCS", {"start": v(61.05, 28.38) * mm, "end": v(79.05, 10.38) * mm});
            skLineSegment(sketch, "E99.MirrorCS", {"start": v(109.05, -1.62) * mm, "end": v(109.05, 10.38) * mm});
            skLineSegment(sketch, "E100.MirrorCS", {"start": v(79.05, 10.38) * mm, "end": v(79.05, -1.62) * mm});
            skCircle(sketch, "E101.MirrorC", {"center": v(94.05, -1.62) * mm, "radius": 6 * mm});
            skSolve(sketch);
        }
        {
            var Q0;
            {var subQ13=sQuery(id+"F16.wireOp",EDGE,"E90.0");Q0=makeQuery(id+"F16.imprint","IMPRINT",FACE,{"disambiguationData":[TD([[makeQuery(id+"F16.imprint","IMPRINT",EDGE,{"derivedFrom":subQ13}),1.0]])]});}
            var Q1;
            {var subQ13=sQuery(id+"F16.wireOp",EDGE,"E91.2");Q1=makeQuery(id+"F16.imprint","IMPRINT",FACE,{"disambiguationData":[TD([[makeQuery(id+"F16.imprint","IMPRINT",EDGE,{"derivedFrom":subQ13}),1.0]])]});}
            var Q2;
            Q2=makeQuery(id+"F16.imprint","IMPRINT",FACE,{"disambiguationData":[TD([[makeQuery(id+"F16.imprint","IMPRINT",EDGE,{"derivedFrom":sQuery(id+"F16.wireOp",EDGE,"E79")}),-1.0]])]});
            var Q3;
            Q3=makeQuery(id+"F16.imprint","IMPRINT",FACE,{"disambiguationData":[TD([[makeQuery(id+"F16.imprint","IMPRINT",EDGE,{"derivedFrom":sQuery(id+"F16.wireOp",EDGE,"E95.MirrorCS")}),-1.0]])]});
            extrude(context, id + "F17", {"entities" : qUnion([Q0, Q1, Q2, Q3]), "depth" : 3 * mm});
        }
    });
